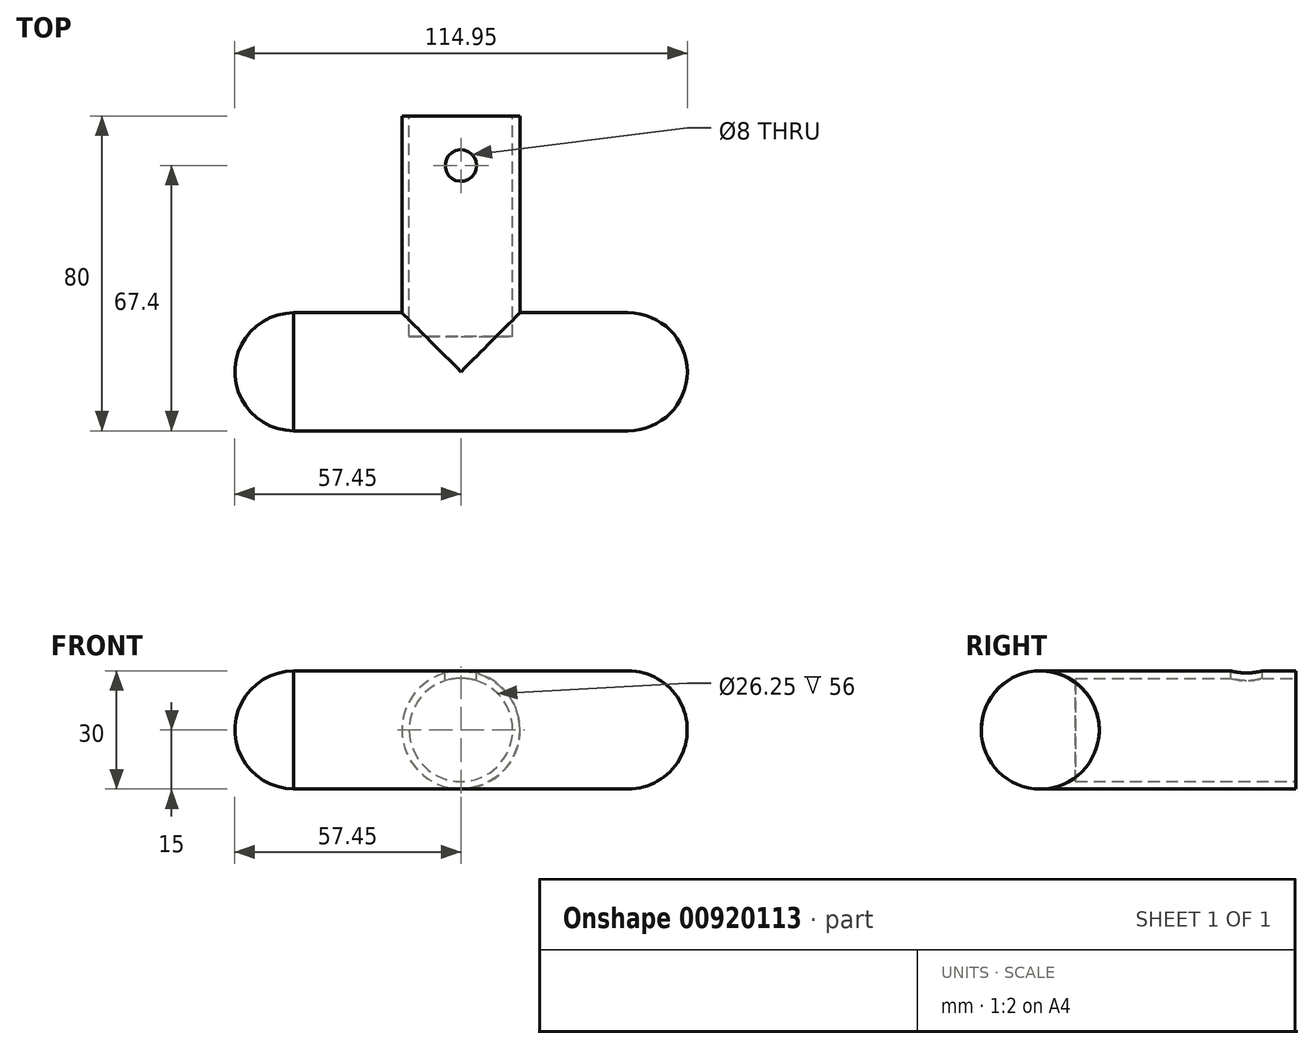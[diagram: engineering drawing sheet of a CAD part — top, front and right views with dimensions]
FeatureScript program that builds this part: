
annotation { "Feature Type Name" : "Feature", "Feature Type Description" : "" }
export const myFeature = defineFeature(function(context is Context, id is Id, definition is map)
    precondition{}
    {
        {
            var Q0;
            Q0=qCreatedBy(makeId("Right.planeOp"),FACE);
            var sketch = newSketch(context, id + "F0", { "sketchPlane" : qUnion([Q0])});
            skCircle(sketch, "E0", {"center": v(0, 0) * mm, "radius": 15 * mm});
            skSolve(sketch);
        }
        {
            var Q0;
            Q0 = qSketchRegion(id + "F0", true);
            extrude(context, id + "F1", {"entities" : qUnion([Q0]), "endBound" : BoundingType.SYMMETRIC, "depth" : 85 * mm, "offsetDistance" : 25 * mm});
        }
        {
            var Q0;
            Q0=qCreatedBy(makeId("Front.planeOp"),FACE);
            var sketch = newSketch(context, id + "F2", { "sketchPlane" : qUnion([Q0])});
            skArc(sketch, "E1", {"start": v(-42.5, 15) * mm, "mid": v(-57.5, 0) * mm, "end": v(-42.5, -15) * mm});
            skArc(sketch, "E2", {"start": v(42.5, -15) * mm, "mid": v(57.5, 0) * mm, "end": v(42.5, 15) * mm});
            skSolve(sketch);
        }
        {
            var Q0;
            Q0=makeQuery(id+"F1.opExtrude","CAP_FACE",FACE,{"disambiguationData":[OSD([sQuery(id+"F0.wireOp",EDGE,"E0")])],"isStart":false});
            var sketch = newSketch(context, id + "F3", { "sketchPlane" : qUnion([Q0])});
            skLineSegment(sketch, "E3", {"start": v(-15, 0) * mm, "end": v(15, 0) * mm});
            skArc(sketch, "E4", {"start": v(15, 0) * mm, "mid": v(0, 15.03) * mm, "end": v(-15, 0) * mm});
            skSolve(sketch);
        }
        {
            var Q0;
            {var subQ0=sQuery(id+"F3.wireOp",EDGE,"E3");Q0=makeQuery(id+"F3.imprint","IMPRINT",FACE,{"disambiguationData":[TD([[makeQuery(id+"F3.imprint","IMPRINT",EDGE,{"derivedFrom":subQ0}),1.0]])]});}
            var Q1;
            Q1=sQuery(id+"F2.wireOp",EDGE,"E2");
            sweep(context, id + "F4", {"operationType" : NewBodyOperationType.ADD, "profiles" : qUnion([Q0]), "path" : qUnion([Q1])});
        }
        {
            var Q0;
            Q0=makeQuery(id+"F1.opExtrude","CAP_FACE",FACE,{"disambiguationData":[OSD([sQuery(id+"F0.wireOp",EDGE,"E0")])],"isStart":true});
            var sketch = newSketch(context, id + "F5", { "sketchPlane" : qUnion([Q0])});
            skLineSegment(sketch, "E5", {"start": v(-15, 0) * mm, "end": v(15, 0) * mm});
            skArc(sketch, "E6", {"start": v(15, 0) * mm, "mid": v(0, 14.95) * mm, "end": v(-15, 0) * mm});
            skSolve(sketch);
        }
        {
            var Q0;
            Q0=makeQuery(id+"F5.imprint","IMPRINT",FACE,{"disambiguationData":[TD([[makeQuery(id+"F5.imprint","IMPRINT",EDGE,{"derivedFrom":sQuery(id+"F5.wireOp",EDGE,"E5")}),1.0]])]});
            var Q1;
            Q1=sQuery(id+"F2.wireOp",EDGE,"E1");
            sweep(context, id + "F6", {"operationType" : NewBodyOperationType.ADD, "profiles" : qUnion([Q0]), "path" : qUnion([Q1])});
        }
        {
            var Q0;
            Q0=qCreatedBy(makeId("Front.planeOp"),FACE);
            var sketch = newSketch(context, id + "F7", { "sketchPlane" : qUnion([Q0])});
            skCircle(sketch, "E7", {"center": v(0, 0) * mm, "radius": 15 * mm});
            skSolve(sketch);
        }
        {
            var Q0;
            Q0 = qSketchRegion(id + "F7", true);
            extrude(context, id + "F8", {"entities" : qUnion([Q0]), "operationType" : NewBodyOperationType.ADD, "oppositeDirection" : true, "depth" : 30 * mm, "offsetDistance" : 25 * mm});
        }
        {
            var Q0;
            Q0=makeQuery(id+"F8.opExtrude","CAP_FACE",FACE,{"disambiguationData":[OSD([sQuery(id+"F7.wireOp",EDGE,"E7")])],"isStart":false});
            var sketch = newSketch(context, id + "F9", { "sketchPlane" : qUnion([Q0])});
            skCircle(sketch, "E8", {"center": v(0, 0) * mm, "radius": 15 * mm});
            skSolve(sketch);
        }
        {
            var Q0;
            Q0 = qSketchRegion(id + "F9", true);
            extrude(context, id + "F10", {"entities" : qUnion([Q0]), "operationType" : NewBodyOperationType.ADD, "depth" : 35 * mm, "offsetDistance" : 25 * mm});
        }
        {
            var Q0;
            Q0=qCreatedBy(makeId("Top.planeOp"),FACE);
            cPlane(context, id + "F11", {"entities" : qUnion([Q0]), "cplaneType" : CPlaneType.OFFSET, "offset" : 15 * mm, "width" : 150 * mm, "height" : 150 * mm});
        }
        {
            var Q0;
            Q0=qCreatedBy(id+"F11.planeOp",FACE);
            var sketch = newSketch(context, id + "F12", { "sketchPlane" : qUnion([Q0])});
            skCircle(sketch, "E9", {"center": v(0, 52.4) * mm, "radius": 4 * mm});
            skSolve(sketch);
        }
        {
            var Q0;
            Q0 = qSketchRegion(id + "F12", true);
            extrude(context, id + "F13", {"entities" : qUnion([Q0]), "operationType" : NewBodyOperationType.REMOVE, "oppositeDirection" : true, "depth" : 25 * mm, "offsetDistance" : 25 * mm});
        }
        {
            var Q0;
            Q0=makeQuery(id+"F10.opExtrude","CAP_FACE",FACE,{"disambiguationData":[OSD([sQuery(id+"F9.wireOp",EDGE,"E8")])],"isStart":false});
            var sketch = newSketch(context, id + "F14", { "sketchPlane" : qUnion([Q0])});
            skCircle(sketch, "E10", {"center": v(0, 0) * mm, "radius": 13.12 * mm});
            skSolve(sketch);
        }
        {
            var Q0;
            Q0 = qSketchRegion(id + "F14", true);
            extrude(context, id + "F15", {"entities" : qUnion([Q0]), "operationType" : NewBodyOperationType.REMOVE, "oppositeDirection" : true, "depth" : 56 * mm, "offsetDistance" : 25 * mm});
        }
    });
